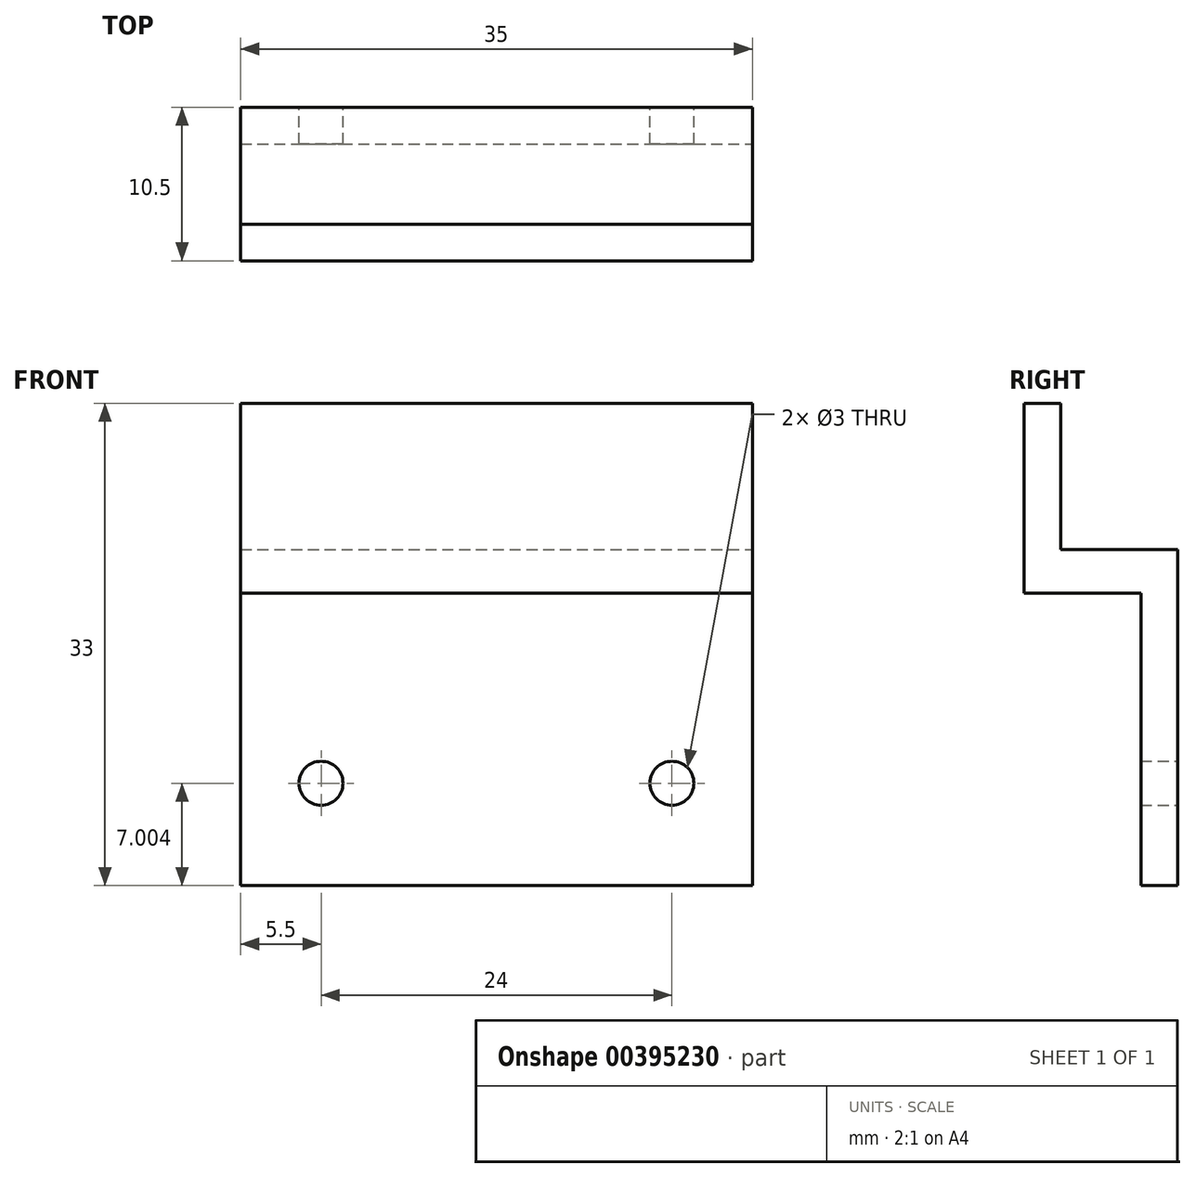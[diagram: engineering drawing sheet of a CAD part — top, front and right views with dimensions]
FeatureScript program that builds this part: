
annotation { "Feature Type Name" : "Feature", "Feature Type Description" : "" }
export const myFeature = defineFeature(function(context is Context, id is Id, definition is map)
    precondition{}
    {
        {
            var Q0;
            Q0=qCreatedBy(makeId("Front.planeOp"),FACE);
            var sketch = newSketch(context, id + "F0", { "sketchPlane" : qUnion([Q0])});
            skLineSegment(sketch, "E0.bottom", {"start": v(-12.95, 15.83) * mm, "end": v(22.05, 15.83) * mm});
            skLineSegment(sketch, "E0.top", {"start": v(-12.95, -4.17) * mm, "end": v(22.05, -4.17) * mm});
            skLineSegment(sketch, "E0.left", {"start": v(-12.95, 15.83) * mm, "end": v(-12.95, -4.17) * mm});
            skLineSegment(sketch, "E0.right", {"start": v(22.05, 15.83) * mm, "end": v(22.05, -4.17) * mm});
            skCircle(sketch, "E1", {"center": v(-7.45, 2.83) * mm, "radius": 1.5 * mm});
            skCircle(sketch, "E2", {"center": v(16.55, 2.83) * mm, "radius": 1.5 * mm});
            skSolve(sketch);
        }
        {
            var Q0;
            Q0=makeQuery(id+"F0.imprint","IMPRINT",FACE,{"disambiguationData":[TD([[makeQuery(id+"F0.imprint","IMPRINT",EDGE,{"derivedFrom":sQuery(id+"F0.wireOp",EDGE,"E0.bottom")}),-1.0]])]});
            extrude(context, id + "F1", {"entities" : qUnion([Q0]), "depth" : 2.5 * mm});
        }
        {
            var Q0;
            Q0=makeQuery(id+"F1.opExtrude","SWEPT_FACE",FACE,{"disambiguationData":[OSD([sQuery(id+"F0.wireOp",EDGE,"E0.bottom")])]});
            var sketch = newSketch(context, id + "F2", { "sketchPlane" : qUnion([Q0])});
            skLineSegment(sketch, "E3.bottom", {"start": v(-12.95, 0) * mm, "end": v(22.05, 0) * mm});
            skLineSegment(sketch, "E3.top", {"start": v(-12.95, -10.5) * mm, "end": v(22.05, -10.5) * mm});
            skLineSegment(sketch, "E3.left", {"start": v(-12.95, 0) * mm, "end": v(-12.95, -10.5) * mm});
            skLineSegment(sketch, "E3.right", {"start": v(22.05, 0) * mm, "end": v(22.05, -10.5) * mm});
            skSolve(sketch);
        }
        {
            var Q0;
            {var subQ0=sQuery(id+"F2.wireOp",EDGE,"E3.top");Q0=makeQuery(id+"F2.imprint","IMPRINT",FACE,{"disambiguationData":[TD([[makeQuery(id+"F2.imprint","IMPRINT",EDGE,{"derivedFrom":subQ0}),1.0]])]});}
            var Q1;
            {var subQ0=sQuery(id+"F2.wireOp",EDGE,"E3.bottom");Q1=makeQuery(id+"F2.imprint","IMPRINT",FACE,{"disambiguationData":[TD([[makeQuery(id+"F2.imprint","IMPRINT",EDGE,{"derivedFrom":subQ0}),-1.0]])]});}
            extrude(context, id + "F3", {"entities" : qUnion([Q0, Q1]), "operationType" : NewBodyOperationType.ADD, "depth" : 3 * mm});
        }
        {
            var Q0;
            Q0=makeQuery(id+"F3.opExtrude","CAP_FACE",FACE,{"disambiguationData":[OSD([sQuery(id+"F2.wireOp",EDGE,"E3.bottom"),sQuery(id+"F2.wireOp",EDGE,"E3.top"),sQuery(id+"F2.wireOp",EDGE,"E3.left"),sQuery(id+"F2.wireOp",EDGE,"E3.right")])],"isStart":false});
            var sketch = newSketch(context, id + "F4", { "sketchPlane" : qUnion([Q0])});
            skLineSegment(sketch, "E4.bottom", {"start": v(-12.95, -10.5) * mm, "end": v(22.05, -10.5) * mm});
            skLineSegment(sketch, "E4.top", {"start": v(-12.95, -8) * mm, "end": v(22.05, -8) * mm});
            skLineSegment(sketch, "E4.left", {"start": v(-12.95, -10.5) * mm, "end": v(-12.95, -8) * mm});
            skLineSegment(sketch, "E4.right", {"start": v(22.05, -10.5) * mm, "end": v(22.05, -8) * mm});
            skSolve(sketch);
        }
        {
            var Q0;
            Q0=makeQuery(id+"F4.imprint","IMPRINT",FACE,{"disambiguationData":[TD([[makeQuery(id+"F4.imprint","IMPRINT",EDGE,{"derivedFrom":sQuery(id+"F4.wireOp",EDGE,"E4.bottom")}),1.0]])]});
            extrude(context, id + "F5", {"entities" : qUnion([Q0]), "operationType" : NewBodyOperationType.ADD, "depth" : 10 * mm});
        }
    });
